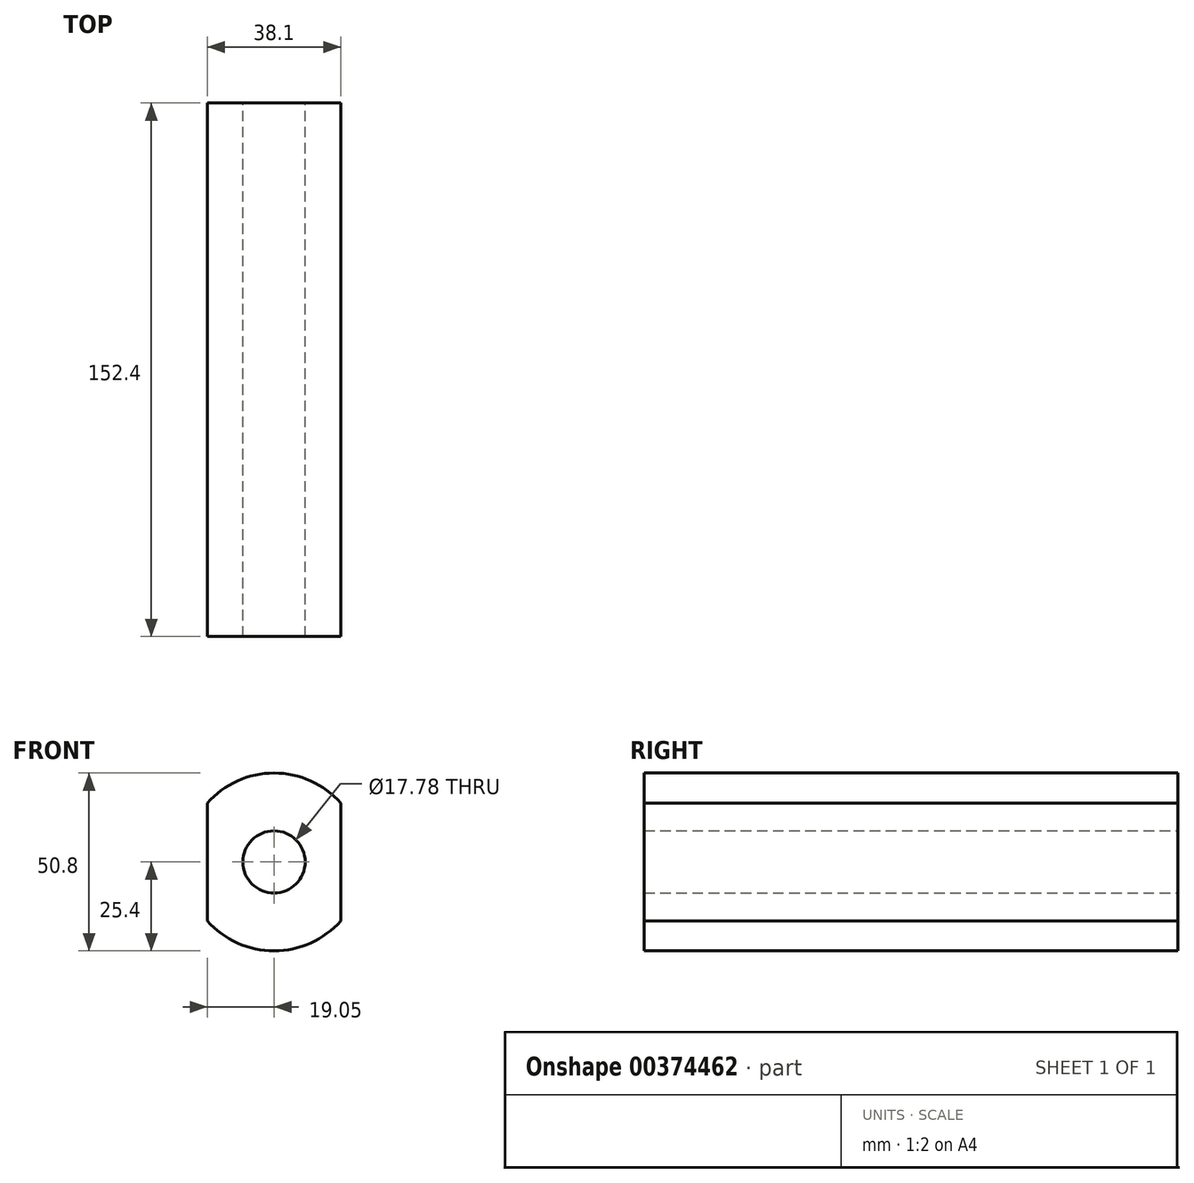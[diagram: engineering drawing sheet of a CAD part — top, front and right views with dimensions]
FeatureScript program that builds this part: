
annotation { "Feature Type Name" : "Feature", "Feature Type Description" : "" }
export const myFeature = defineFeature(function(context is Context, id is Id, definition is map)
    precondition{}
    {
        {
            var Q0;
            Q0=qCreatedBy(makeId("Front.planeOp"),FACE);
            var sketch = newSketch(context, id + "F0", { "sketchPlane" : qUnion([Q0])});
            skLineSegment(sketch, "E0.bottom", {"start": v(0, 0) * mm, "end": v(38.1, 0) * mm});
            skLineSegment(sketch, "E0.top", {"start": v(0, 50.8) * mm, "end": v(38.1, 50.8) * mm});
            skLineSegment(sketch, "E0.left", {"start": v(0, 0) * mm, "end": v(0, 50.8) * mm});
            skLineSegment(sketch, "E0.right", {"start": v(38.1, 0) * mm, "end": v(38.1, 50.8) * mm});
            skSolve(sketch);
        }
        {
            var Q0;
            Q0 = qSketchRegion(id + "F0", true);
            extrude(context, id + "F1", {"entities" : qUnion([Q0]), "depth" : 152.4 * mm});
        }
        {
            var Q0;
            Q0=makeQuery(id+"F1.opExtrude","CAP_FACE",FACE,{"disambiguationData":[OSD([sQuery(id+"F0.wireOp",EDGE,"E0.bottom"),sQuery(id+"F0.wireOp",EDGE,"E0.top"),sQuery(id+"F0.wireOp",EDGE,"E0.left"),sQuery(id+"F0.wireOp",EDGE,"E0.right")])],"isStart":true});
            var sketch = newSketch(context, id + "F2", { "sketchPlane" : qUnion([Q0])});
            skCircle(sketch, "E1", {"center": v(-19.05, 25.4) * mm, "radius": 8.9 * mm});
            skLineSegment(sketch, "E2", {"start": v(-19.05, 25.4) * mm, "end": v(-19.05, 50.8) * mm, "construction": true});
            skSolve(sketch);
        }
        {
            var Q0;
            Q0 = qSketchRegion(id + "F2", true);
            extrude(context, id + "F3", {"entities" : qUnion([Q0]), "operationType" : NewBodyOperationType.REMOVE, "endBound" : BoundingType.THROUGH_ALL, "oppositeDirection" : true, "depth" : 25.4 * mm, "offsetDistance" : 25.4 * mm});
        }
        {
            var Q0;
            Q0=qCreatedBy(makeId("Right.planeOp"),FACE);
            cPlane(context, id + "F4", {"entities" : qUnion([Q0]), "cplaneType" : CPlaneType.OFFSET, "offset" : 19.05 * mm, "width" : 152.4 * mm, "height" : 152.4 * mm});
        }
        {
            var Q0;
            Q0=qCreatedBy(id+"F4.planeOp",FACE);
            var sketch = newSketch(context, id + "F5", { "sketchPlane" : qUnion([Q0])});
            skLineSegment(sketch, "E3.bottom", {"start": v(-152.4, 50.8) * mm, "end": v(0, 50.8) * mm});
            skLineSegment(sketch, "E3.top", {"start": v(-152.4, 79.21) * mm, "end": v(0, 79.21) * mm});
            skLineSegment(sketch, "E3.left", {"start": v(-152.4, 50.8) * mm, "end": v(-152.4, 79.21) * mm});
            skLineSegment(sketch, "E3.right", {"start": v(0, 50.8) * mm, "end": v(0, 79.21) * mm});
            skLineSegment(sketch, "E4", {"start": v(-152.4, 25.4) * mm, "end": v(0, 25.4) * mm, "construction": true});
            skSolve(sketch);
        }
        {
            var Q0;
            Q0=makeQuery(id+"F5.imprint","IMPRINT",FACE,{"disambiguationData":[TD([[makeQuery(id+"F5.imprint","IMPRINT",EDGE,{"derivedFrom":sQuery(id+"F5.wireOp",EDGE,"E3.bottom")}),1.0]])]});
            var Q1;
            Q1=sQuery(id+"F5.wireOp",EDGE,"E4");
            var Q2;
            Q2=sQuery(id+"F5.wireOp",EDGE,"E3.top");
            var Q3;
            Q3=sQuery(id+"F5.wireOp",EDGE,"E3.left");
            var Q4;
            Q4=sQuery(id+"F5.wireOp",EDGE,"E3.bottom");
            var Q5;
            Q5=sQuery(id+"F5.wireOp",EDGE,"E3.right");
            var Q6;
            Q6=sQuery(id+"F5.wireOp",EDGE,"E4");
            revolve(context, id + "F6", {"operationType" : NewBodyOperationType.REMOVE, "entities" : qUnion([Q0]), "surfaceEntities" : qUnion([Q1, Q2, Q3, Q4, Q5]), "axis" : qUnion([Q6]), "revolveType" : RevolveType.FULL, "oppositeDirection" : true});
        }
    });
